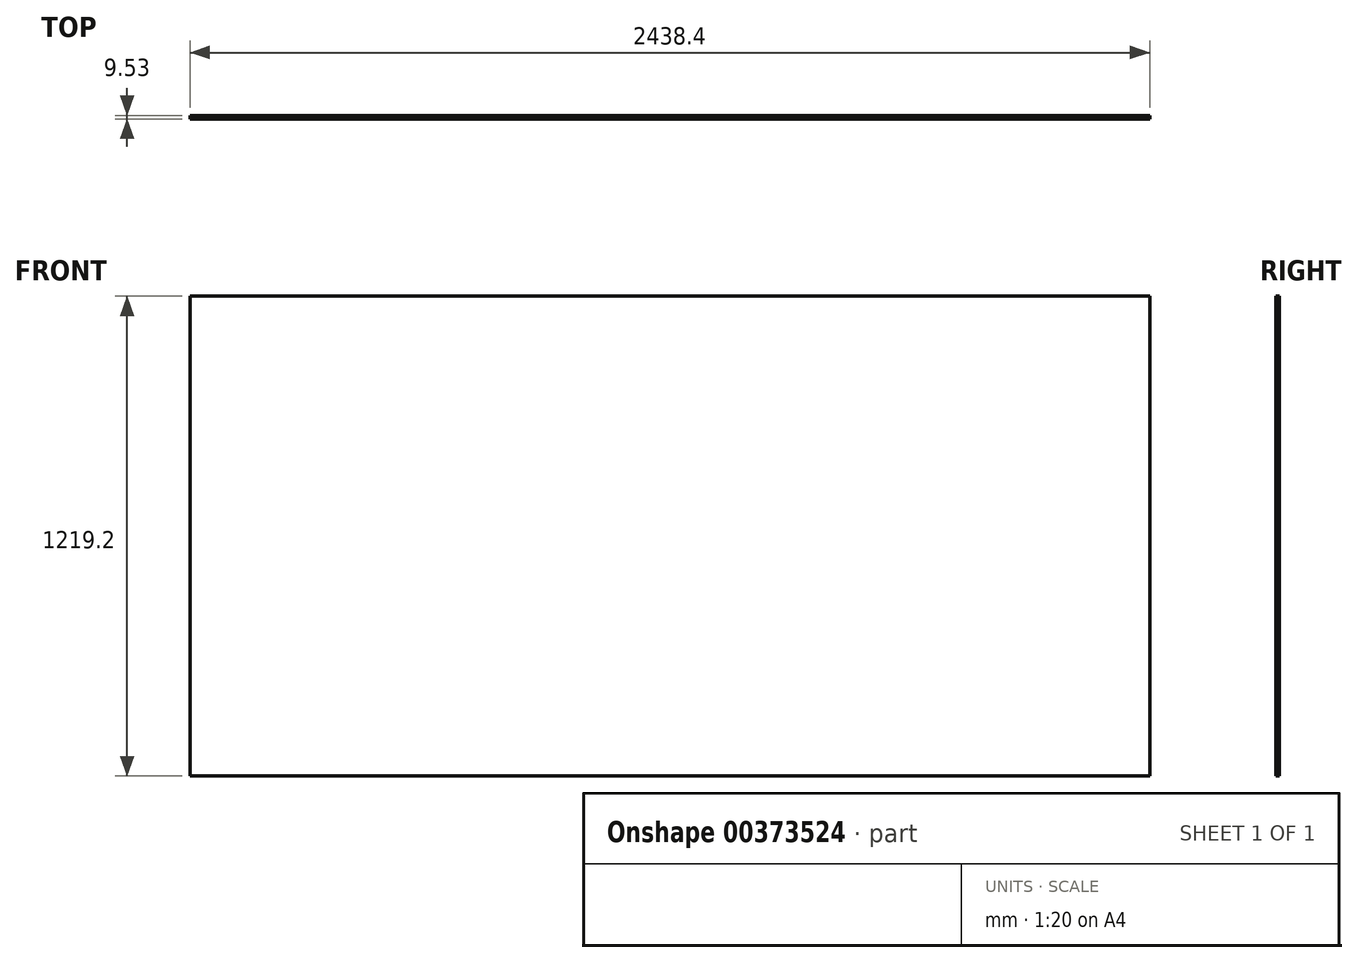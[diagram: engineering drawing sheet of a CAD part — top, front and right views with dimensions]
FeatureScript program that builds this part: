
annotation { "Feature Type Name" : "Feature", "Feature Type Description" : "" }
export const myFeature = defineFeature(function(context is Context, id is Id, definition is map)
    precondition{}
    {
        {
            var Q0;
            Q0=qCreatedBy(makeId("Front.planeOp"),FACE);
            var sketch = newSketch(context, id + "F0", { "sketchPlane" : qUnion([Q0])});
            skLineSegment(sketch, "E0.bottom", {"start": v(-2395.66, 1183.94) * mm, "end": v(42.74, 1183.94) * mm});
            skLineSegment(sketch, "E0.top", {"start": v(-2395.66, -35.26) * mm, "end": v(42.74, -35.26) * mm});
            skLineSegment(sketch, "E0.left", {"start": v(-2395.66, 1183.94) * mm, "end": v(-2395.66, -35.26) * mm});
            skLineSegment(sketch, "E0.right", {"start": v(42.74, 1183.94) * mm, "end": v(42.74, -35.26) * mm});
            skSolve(sketch);
        }
        {
            var Q0;
            Q0=makeQuery(id+"F0.imprint","IMPRINT",FACE,{"disambiguationData":[TD([[makeQuery(id+"F0.imprint","IMPRINT",EDGE,{"derivedFrom":sQuery(id+"F0.wireOp",EDGE,"E0.bottom")}),-1.0]])]});
            extrude(context, id + "F1", {"entities" : qUnion([Q0]), "depth" : 9.52 * mm});
        }
    });
